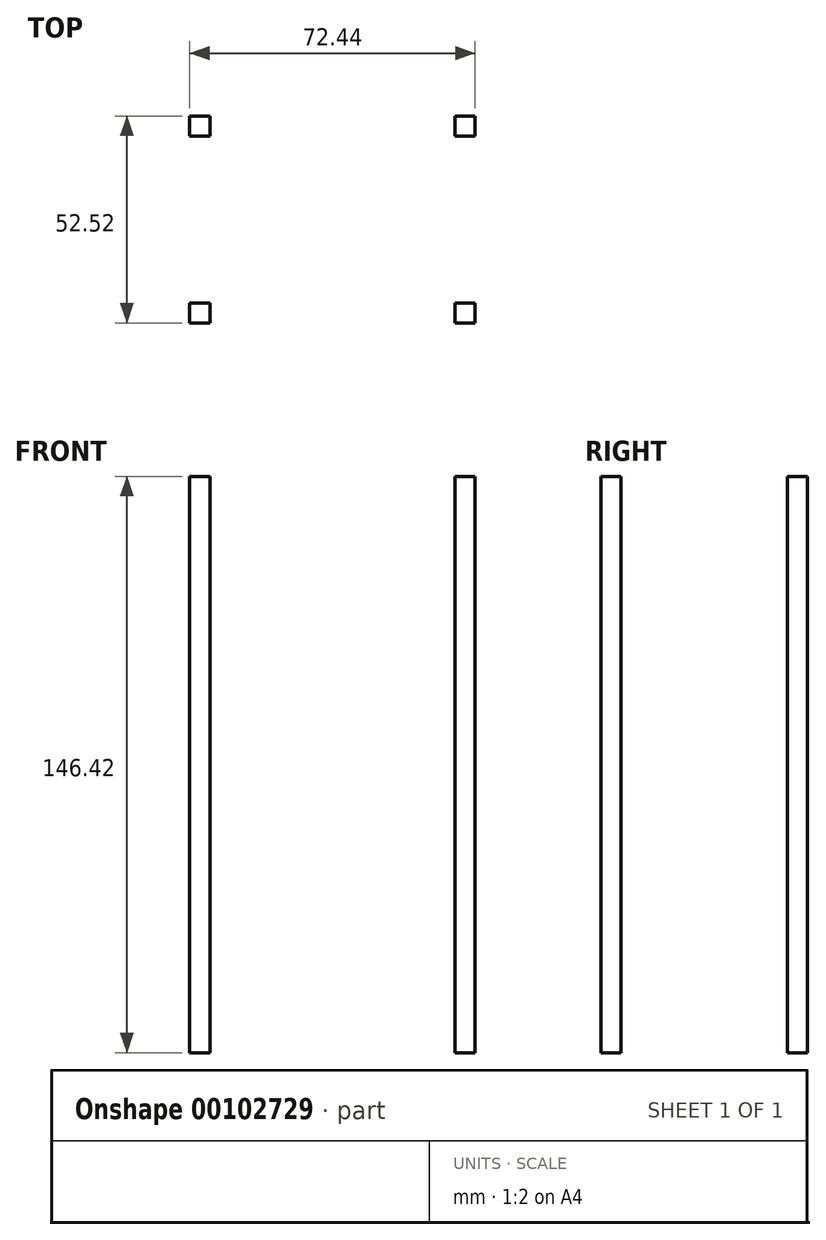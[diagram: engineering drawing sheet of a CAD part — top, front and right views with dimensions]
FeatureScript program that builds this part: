
annotation { "Feature Type Name" : "Feature", "Feature Type Description" : "" }
export const myFeature = defineFeature(function(context is Context, id is Id, definition is map)
    precondition{}
    {
        {
            var Q0;
            Q0=qCreatedBy(makeId("Top.planeOp"),FACE);
            var sketch = newSketch(context, id + "F0", { "sketchPlane" : qUnion([Q0])});
            skLineSegment(sketch, "E0.bottom", {"start": v(-36.22, 26.26) * mm, "end": v(-31.14, 26.26) * mm});
            skLineSegment(sketch, "E0.top", {"start": v(-36.22, 21.18) * mm, "end": v(-31.14, 21.18) * mm});
            skLineSegment(sketch, "E0.left", {"start": v(-36.22, 26.26) * mm, "end": v(-36.22, 21.18) * mm});
            skLineSegment(sketch, "E0.right", {"start": v(-31.14, 26.26) * mm, "end": v(-31.14, 21.18) * mm});
            skLineSegment(sketch, "E1.MirrorCS", {"start": v(-36.22, -26.26) * mm, "end": v(-31.14, -26.26) * mm});
            skLineSegment(sketch, "E2.MirrorCS", {"start": v(-36.22, -21.18) * mm, "end": v(-31.14, -21.18) * mm});
            skLineSegment(sketch, "E3.MirrorCS", {"start": v(-31.14, -26.26) * mm, "end": v(-31.14, -21.18) * mm});
            skLineSegment(sketch, "E4.MirrorCS", {"start": v(-36.22, -26.26) * mm, "end": v(-36.22, -21.18) * mm});
            skLineSegment(sketch, "E5.MirrorCS", {"start": v(36.22, -26.26) * mm, "end": v(36.22, -21.18) * mm});
            skLineSegment(sketch, "E6.MirrorCS", {"start": v(36.22, 26.26) * mm, "end": v(31.14, 26.26) * mm});
            skLineSegment(sketch, "E7.MirrorCS", {"start": v(36.22, 21.18) * mm, "end": v(31.14, 21.18) * mm});
            skLineSegment(sketch, "E8.MirrorCS", {"start": v(36.22, 26.26) * mm, "end": v(36.22, 21.18) * mm});
            skLineSegment(sketch, "E9.MirrorCS", {"start": v(31.14, 26.26) * mm, "end": v(31.14, 21.18) * mm});
            skLineSegment(sketch, "E10.MirrorCS", {"start": v(36.22, -26.26) * mm, "end": v(31.14, -26.26) * mm});
            skLineSegment(sketch, "E11.MirrorCS", {"start": v(36.22, -21.18) * mm, "end": v(31.14, -21.18) * mm});
            skLineSegment(sketch, "E12.MirrorCS", {"start": v(31.14, -26.26) * mm, "end": v(31.14, -21.18) * mm});
            skSolve(sketch);
        }
        {
            var Q0;
            Q0 = qSketchRegion(id + "F0", true);
            extrude(context, id + "F1", {"entities" : qUnion([Q0]), "depth" : 146.42 * mm});
        }
        {
            var Q0;
            Q0=qCreatedBy(makeId("Top.planeOp"),FACE);
            var sketch = newSketch(context, id + "F2", { "sketchPlane" : qUnion([Q0])});
            skLineSegment(sketch, "E13.bottom", {"start": v(36.27, 26.44) * mm, "end": v(-36.34, 26.44) * mm});
            skLineSegment(sketch, "E13.top", {"start": v(36.27, -26.11) * mm, "end": v(-36.34, -26.11) * mm});
            skLineSegment(sketch, "E13.left", {"start": v(36.27, 26.44) * mm, "end": v(36.27, -26.11) * mm});
            skLineSegment(sketch, "E13.right", {"start": v(-36.34, 26.44) * mm, "end": v(-36.34, -26.11) * mm});
            skSolve(sketch);
        }
        {
            var Q0;
            Q0=makeQuery(id+"F2.imprint","IMPRINT",FACE,{"disambiguationData":[TD([[makeQuery(id+"F2.imprint","IMPRINT",EDGE,{"derivedFrom":sQuery(id+"F2.wireOp",EDGE,"E13.bottom")}),1.0]])]});
            var sketch = newSketch(context, id + "F3", { "sketchPlane" : qUnion([Q0])});
            skLineSegment(sketch, "E14", {"start": v(36.27, 26.76) * mm, "end": v(-36.34, 26.76) * mm});
            skSolve(sketch);
        }
        {
            var Q0;
            Q0 = qSketchRegion(id + "F3", true);
            var Q1;
            Q1=sQuery(id+"F3.wireOp",EDGE,"E14");
            extrude(context, id + "F4", {"entities" : qUnion([Q0]), "bodyType" : ToolBodyType.SURFACE, "surfaceEntities" : qUnion([Q1]), "oppositeDirection" : true, "depth" : 49.15 * mm});
        }
    });
